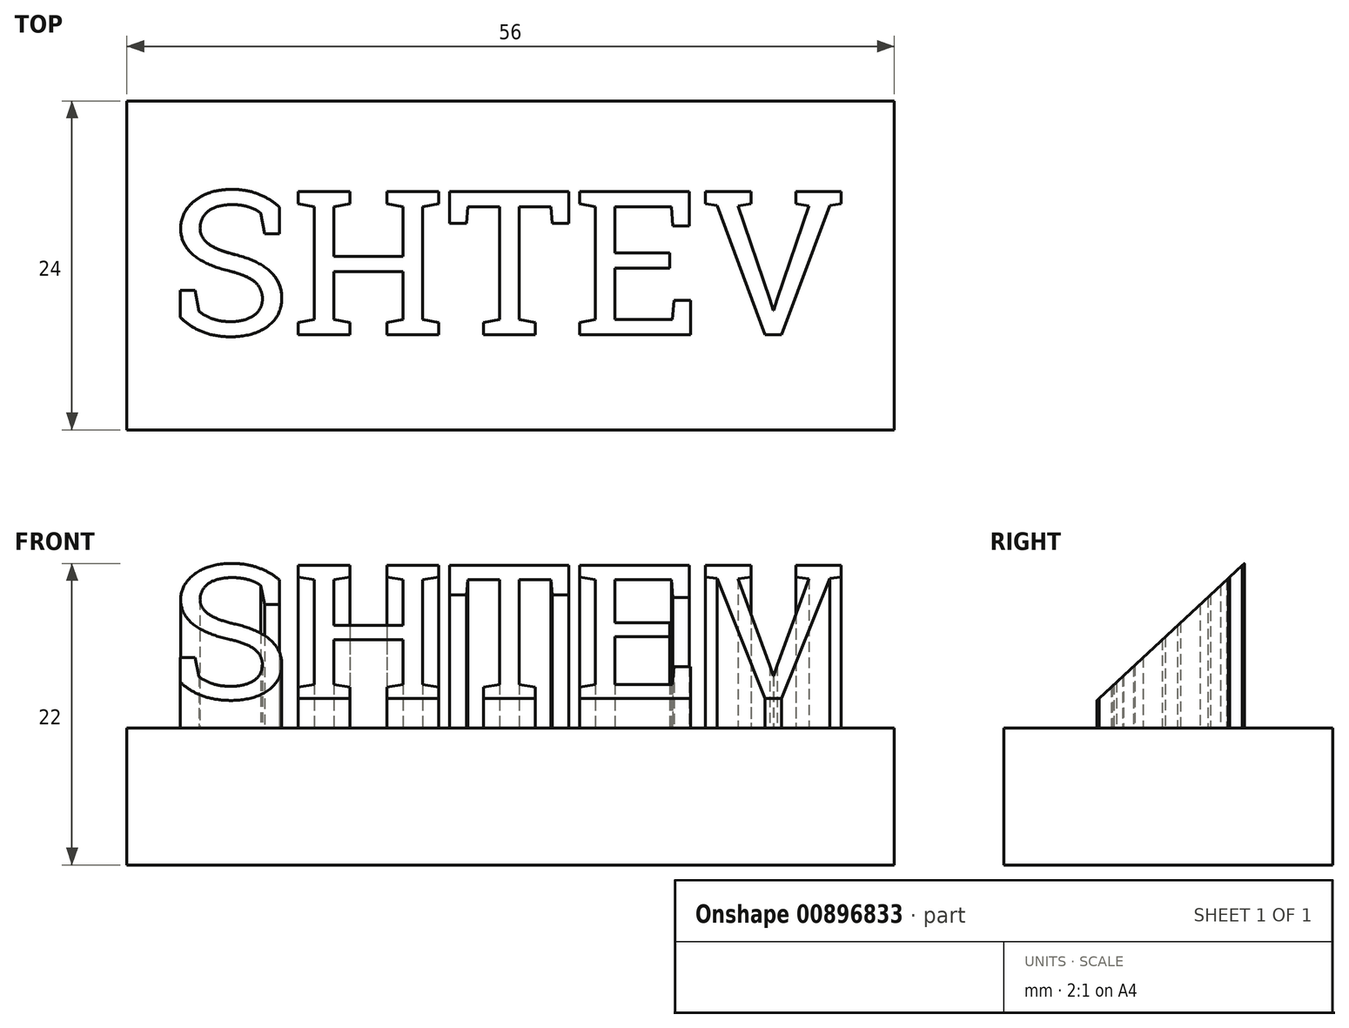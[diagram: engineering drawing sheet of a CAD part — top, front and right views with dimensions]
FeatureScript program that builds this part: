
annotation { "Feature Type Name" : "Feature", "Feature Type Description" : "" }
export const myFeature = defineFeature(function(context is Context, id is Id, definition is map)
    precondition{}
    {
        {
            var Q0;
            Q0=qCreatedBy(makeId("Top.planeOp"),FACE);
            var sketch = newSketch(context, id + "F0", { "sketchPlane" : qUnion([Q0])});
            skLineSegment(sketch, "E0.bottom", {"start": v(31.66, -15) * mm, "end": v(-28.34, -15) * mm});
            skLineSegment(sketch, "E0.top", {"start": v(31.66, 15) * mm, "end": v(-28.34, 15) * mm});
            skLineSegment(sketch, "E0.left", {"start": v(31.66, -15) * mm, "end": v(31.66, 15) * mm});
            skLineSegment(sketch, "E0.right", {"start": v(-28.34, -15) * mm, "end": v(-28.34, 15) * mm});
            skPoint(sketch, "E0.middle", {"position": v(1.66, 0) * mm});
            skSolve(sketch);
        }
        {
            var Q0;
            Q0=makeQuery(id+"F0.imprint","IMPRINT",FACE,{"disambiguationData":[TD([[makeQuery(id+"F0.imprint","IMPRINT",EDGE,{"derivedFrom":sQuery(id+"F0.wireOp",EDGE,"E0.bottom")}),-1.0]])]});
            extrude(context, id + "F1", {"entities" : qUnion([Q0]), "depth" : 10 * mm, "offsetDistance" : 25 * mm});
        }
        {
            var Q0;
            Q0=makeQuery(id+"F1.opExtrude","CAP_FACE",FACE,{"disambiguationData":[OSD([sQuery(id+"F0.wireOp",EDGE,"E0.bottom"),sQuery(id+"F0.wireOp",EDGE,"E0.top"),sQuery(id+"F0.wireOp",EDGE,"E0.left"),sQuery(id+"F0.wireOp",EDGE,"E0.right")])],"isStart":false});
            var sketch = newSketch(context, id + "F2", { "sketchPlane" : qUnion([Q0])});
            skLineSegment(sketch, "E1.0.0", {"start": v(31.66, -15) * mm, "end": v(31.66, 15) * mm});
            skLineSegment(sketch, "E1.0.1", {"start": v(31.66, 15) * mm, "end": v(-28.34, 15) * mm});
            skLineSegment(sketch, "E1.0.2", {"start": v(-28.34, 15) * mm, "end": v(-28.34, -15) * mm});
            skLineSegment(sketch, "E1.0.3", {"start": v(-28.34, -15) * mm, "end": v(31.66, -15) * mm});
            skLineSegment(sketch, "E2", {"start": v(-28.34, 12) * mm, "end": v(31.66, 12) * mm});
            skLineSegment(sketch, "E3", {"start": v(-28.34, -12) * mm, "end": v(31.66, -12) * mm});
            skPoint(sketch, "E3.startSnap0", {"position": v(-14.7, -12) * mm});
            skLineSegment(sketch, "E4", {"start": v(-26.34, -15) * mm, "end": v(-26.34, 15) * mm});
            skLineSegment(sketch, "E5", {"start": v(29.66, 15) * mm, "end": v(29.66, -15) * mm});
            skText(sketch, "E6", { "text": "SHTEV", "fontName": "RobotoSlab-Regular.ttf"});
            skLineSegment(sketch, "E7", {"start": v(1.7, 5.53) * mm, "end": v(1.7, -5.06) * mm, "construction": true});
            const initialGuessF2  = {"E6": [-0.0233, -0.00506, 1, 0, 0.01059]};
            skSetInitialGuess(sketch, initialGuessF2);
            skSolve(sketch);
        }
        {
            var Q0;
            {var subQ0=sQuery(id+"F2.wireOp",EDGE,"E2");var subQ1=sQuery(id+"F2.wireOp",EDGE,"E1.0.2");var subQ2=makeQuery(id+"F2.imprint","INTERSECT",VERTEX,{"derivedFrom":[subQ1,subQ0]});Q0=makeQuery(id+"F2.imprint","IMPRINT",FACE,{"disambiguationData":[TD([[makeQuery(id+"F2.imprint","IMPRINT",EDGE,{"disambiguationData":[TD([[subQ2,1.0]])],"derivedFrom":subQ1}),-1.0]])]});}
            var Q1;
            {var subQ0=sQuery(id+"F2.wireOp",EDGE,"E2");var subQ1=sQuery(id+"F2.wireOp",EDGE,"E1.0.0");var subQ2=makeQuery(id+"F2.imprint","INTERSECT",VERTEX,{"derivedFrom":[subQ1,subQ0]});Q1=makeQuery(id+"F2.imprint","IMPRINT",FACE,{"disambiguationData":[TD([[makeQuery(id+"F2.imprint","IMPRINT",EDGE,{"disambiguationData":[TD([[subQ2,1.0]])],"derivedFrom":subQ1}),1.0]])]});}
            var Q2;
            {var subQ0=sQuery(id+"F2.wireOp",EDGE,"E1.0.3");var subQ1=sQuery(id+"F2.wireOp",EDGE,"E1.0.0");var subQ2=makeQuery(id+"F2.imprint","INTERSECT",VERTEX,{"derivedFrom":[subQ1,subQ0]});Q2=makeQuery(id+"F2.imprint","IMPRINT",FACE,{"disambiguationData":[TD([[makeQuery(id+"F2.imprint","IMPRINT",EDGE,{"disambiguationData":[TD([[subQ2,-1.0]])],"derivedFrom":subQ1}),1.0]])]});}
            var Q3;
            {var subQ0=sQuery(id+"F2.wireOp",EDGE,"E4");var subQ1=sQuery(id+"F2.wireOp",EDGE,"E1.0.3");var subQ2=makeQuery(id+"F2.imprint","INTERSECT",VERTEX,{"derivedFrom":[subQ1,subQ0]});Q3=makeQuery(id+"F2.imprint","IMPRINT",FACE,{"disambiguationData":[TD([[makeQuery(id+"F2.imprint","IMPRINT",EDGE,{"disambiguationData":[TD([[subQ2,1.0]])],"derivedFrom":subQ1}),-1.0]])]});}
            var Q4;
            {var subQ0=sQuery(id+"F2.wireOp",EDGE,"E1.0.3");var subQ1=sQuery(id+"F2.wireOp",EDGE,"E1.0.2");var subQ2=makeQuery(id+"F2.imprint","INTERSECT",VERTEX,{"derivedFrom":[subQ1,subQ0]});Q4=makeQuery(id+"F2.imprint","IMPRINT",FACE,{"disambiguationData":[TD([[makeQuery(id+"F2.imprint","IMPRINT",EDGE,{"disambiguationData":[TD([[subQ2,-1.0]])],"derivedFrom":subQ1}),-1.0]])]});}
            var Q5;
            {var subQ0=sQuery(id+"F2.wireOp",EDGE,"E1.0.1");var subQ1=sQuery(id+"F2.wireOp",EDGE,"E1.0.0");var subQ2=makeQuery(id+"F2.imprint","INTERSECT",VERTEX,{"derivedFrom":[subQ1,subQ0]});Q5=makeQuery(id+"F2.imprint","IMPRINT",FACE,{"disambiguationData":[TD([[makeQuery(id+"F2.imprint","IMPRINT",EDGE,{"disambiguationData":[TD([[subQ2,1.0]])],"derivedFrom":subQ1}),1.0]])]});}
            var Q6;
            {var subQ0=sQuery(id+"F2.wireOp",EDGE,"E4");var subQ1=sQuery(id+"F2.wireOp",EDGE,"E1.0.1");var subQ2=makeQuery(id+"F2.imprint","INTERSECT",VERTEX,{"derivedFrom":[subQ1,subQ0]});Q6=makeQuery(id+"F2.imprint","IMPRINT",FACE,{"disambiguationData":[TD([[makeQuery(id+"F2.imprint","IMPRINT",EDGE,{"disambiguationData":[TD([[subQ2,1.0]])],"derivedFrom":subQ1}),1.0]])]});}
            var Q7;
            {var subQ0=sQuery(id+"F2.wireOp",EDGE,"E1.0.2");var subQ1=sQuery(id+"F2.wireOp",EDGE,"E1.0.1");var subQ2=makeQuery(id+"F2.imprint","INTERSECT",VERTEX,{"derivedFrom":[subQ1,subQ0]});Q7=makeQuery(id+"F2.imprint","IMPRINT",FACE,{"disambiguationData":[TD([[makeQuery(id+"F2.imprint","IMPRINT",EDGE,{"disambiguationData":[TD([[subQ2,1.0]])],"derivedFrom":subQ1}),1.0]])]});}
            extrude(context, id + "F3", {"entities" : qUnion([Q0, Q1, Q2, Q3, Q4, Q5, Q6, Q7]), "operationType" : NewBodyOperationType.REMOVE, "oppositeDirection" : true, "depth" : 25 * mm, "offsetDistance" : 25 * mm});
        }
        {
            var Q0;
            Q0=makeQuery(id+"F2.imprint","IMPRINT",FACE,{"disambiguationData":[TD([[makeQuery(id+"F2.imprint","IMPRINT",EDGE,{"derivedFrom":sQuery(id+"F2.wireOp",EDGE,"E6.sketch_text.stroke-0")}),-1.0]])]});
            var Q1;
            Q1=makeQuery(id+"F2.imprint","IMPRINT",FACE,{"disambiguationData":[TD([[makeQuery(id+"F2.imprint","IMPRINT",EDGE,{"derivedFrom":sQuery(id+"F2.wireOp",EDGE,"E6.sketch_text.stroke-24")}),-1.0]])]});
            var Q2;
            Q2=makeQuery(id+"F2.imprint","IMPRINT",FACE,{"disambiguationData":[TD([[makeQuery(id+"F2.imprint","IMPRINT",EDGE,{"derivedFrom":sQuery(id+"F2.wireOp",EDGE,"E6.sketch_text.stroke-54")}),-1.0]])]});
            var Q3;
            Q3=makeQuery(id+"F2.imprint","IMPRINT",FACE,{"disambiguationData":[TD([[makeQuery(id+"F2.imprint","IMPRINT",EDGE,{"derivedFrom":sQuery(id+"F2.wireOp",EDGE,"E6.sketch_text.stroke-60")}),-1.0]])]});
            var Q4;
            Q4=makeQuery(id+"F2.imprint","IMPRINT",FACE,{"disambiguationData":[TD([[makeQuery(id+"F2.imprint","IMPRINT",EDGE,{"derivedFrom":sQuery(id+"F2.wireOp",EDGE,"E6.sketch_text.stroke-76")}),-1.0]])]});
            var Q5;
            Q5=makeQuery(id+"F2.imprint","IMPRINT",FACE,{"disambiguationData":[TD([[makeQuery(id+"F2.imprint","IMPRINT",EDGE,{"derivedFrom":sQuery(id+"F2.wireOp",EDGE,"E6.sketch_text.stroke-96")}),-1.0]])]});
            extrude(context, id + "F4", {"entities" : qUnion([Q0, Q1, Q2, Q3, Q4, Q5]), "operationType" : NewBodyOperationType.ADD, "depth" : 12 * mm, "offsetDistance" : 25 * mm});
        }
        {
            var Q0;
            Q0=makeQuery(id+"F4.opExtrude","SWEPT_FACE",FACE,{"disambiguationData":[OSD([sQuery(id+"F2.wireOp",EDGE,"E6.sketch_text.stroke-14")])]});
            var sketch = newSketch(context, id + "F5", { "sketchPlane" : qUnion([Q0])});
            skLineSegment(sketch, "E8.0", {"start": v(5.21, 22) * mm, "end": v(5.21, 10) * mm});
            skLineSegment(sketch, "E9.0", {"start": v(-5.54, 22) * mm, "end": v(-5.54, 10) * mm});
            skLineSegment(sketch, "E10", {"start": v(-5.54, 22) * mm, "end": v(5.21, 22) * mm});
            skLineSegment(sketch, "E11", {"start": v(5.21, 10) * mm, "end": v(5.21, 12) * mm});
            skLineSegment(sketch, "E12", {"start": v(-5.54, 22) * mm, "end": v(5.21, 12) * mm});
            skSolve(sketch);
        }
        {
            var Q0;
            {var subQ0=sQuery(id+"F5.wireOp",EDGE,"E10");var subQ1=makeQuery(id+"F4.opExtrude","SWEPT_EDGE",EDGE,{"disambiguationData":[OSD([sQuery(id+"F2.wireOp",EDGE,"E6.sketch_text.stroke-14"),sQuery(id+"F2.wireOp",EDGE,"E6.sketch_text.stroke-15")])]});var subQ2=makeQuery(id+"F5.imprint","INTERSECT",VERTEX,{"derivedFrom":[subQ1,subQ0]});var subQ3=sQuery(id+"F5.wireOp",EDGE,"E12");var subQ4=makeQuery(id+"F5.imprint","INTERSECT",VERTEX,{"derivedFrom":[subQ0,subQ3]});Q0=makeQuery(id+"F5.imprint","IMPRINT",FACE,{"disambiguationData":[TD([[makeQuery(id+"F5.imprint","IMPRINT",EDGE,{"disambiguationData":[TD([[subQ2,1.0],[subQ4,-1.0]])],"derivedFrom":subQ0}),-1.0]])]});}
            var Q1;
            {var subQ0=sQuery(id+"F5.wireOp",EDGE,"E10");var subQ1=sQuery(id+"F2.wireOp",EDGE,"E6.sketch_text.stroke-14");var subQ2=makeQuery(id+"F4.opExtrude","SWEPT_EDGE",EDGE,{"disambiguationData":[OSD([sQuery(id+"F2.wireOp",EDGE,"E6.sketch_text.stroke-13"),subQ1])]});var subQ3=makeQuery(id+"F5.imprint","INTERSECT",VERTEX,{"derivedFrom":[subQ2,subQ0]});var subQ4=makeQuery(id+"F4.opExtrude","SWEPT_EDGE",EDGE,{"disambiguationData":[OSD([subQ1,sQuery(id+"F2.wireOp",EDGE,"E6.sketch_text.stroke-15")])]});var subQ5=makeQuery(id+"F5.imprint","INTERSECT",VERTEX,{"derivedFrom":[subQ4,subQ0]});Q1=makeQuery(id+"F5.imprint","IMPRINT",FACE,{"disambiguationData":[TD([[makeQuery(id+"F5.imprint","IMPRINT",EDGE,{"disambiguationData":[TD([[subQ3,-1.0],[subQ5,1.0]])],"derivedFrom":subQ0}),1.0]])]});}
            var Q2;
            {var subQ0=sQuery(id+"F5.wireOp",EDGE,"E10");var subQ1=sQuery(id+"F5.wireOp",EDGE,"E8.0");var subQ2=makeQuery(id+"F5.imprint","INTERSECT",VERTEX,{"derivedFrom":[subQ1,subQ0]});Q2=makeQuery(id+"F5.imprint","IMPRINT",FACE,{"disambiguationData":[TD([[makeQuery(id+"F5.imprint","IMPRINT",EDGE,{"disambiguationData":[TD([[subQ2,-1.0]])],"derivedFrom":subQ1}),-1.0]])]});}
            extrude(context, id + "F6", {"entities" : qUnion([Q0, Q1, Q2]), "operationType" : NewBodyOperationType.REMOVE, "oppositeDirection" : true, "depth" : 50 * mm, "offsetDistance" : 25 * mm});
        }
    });
